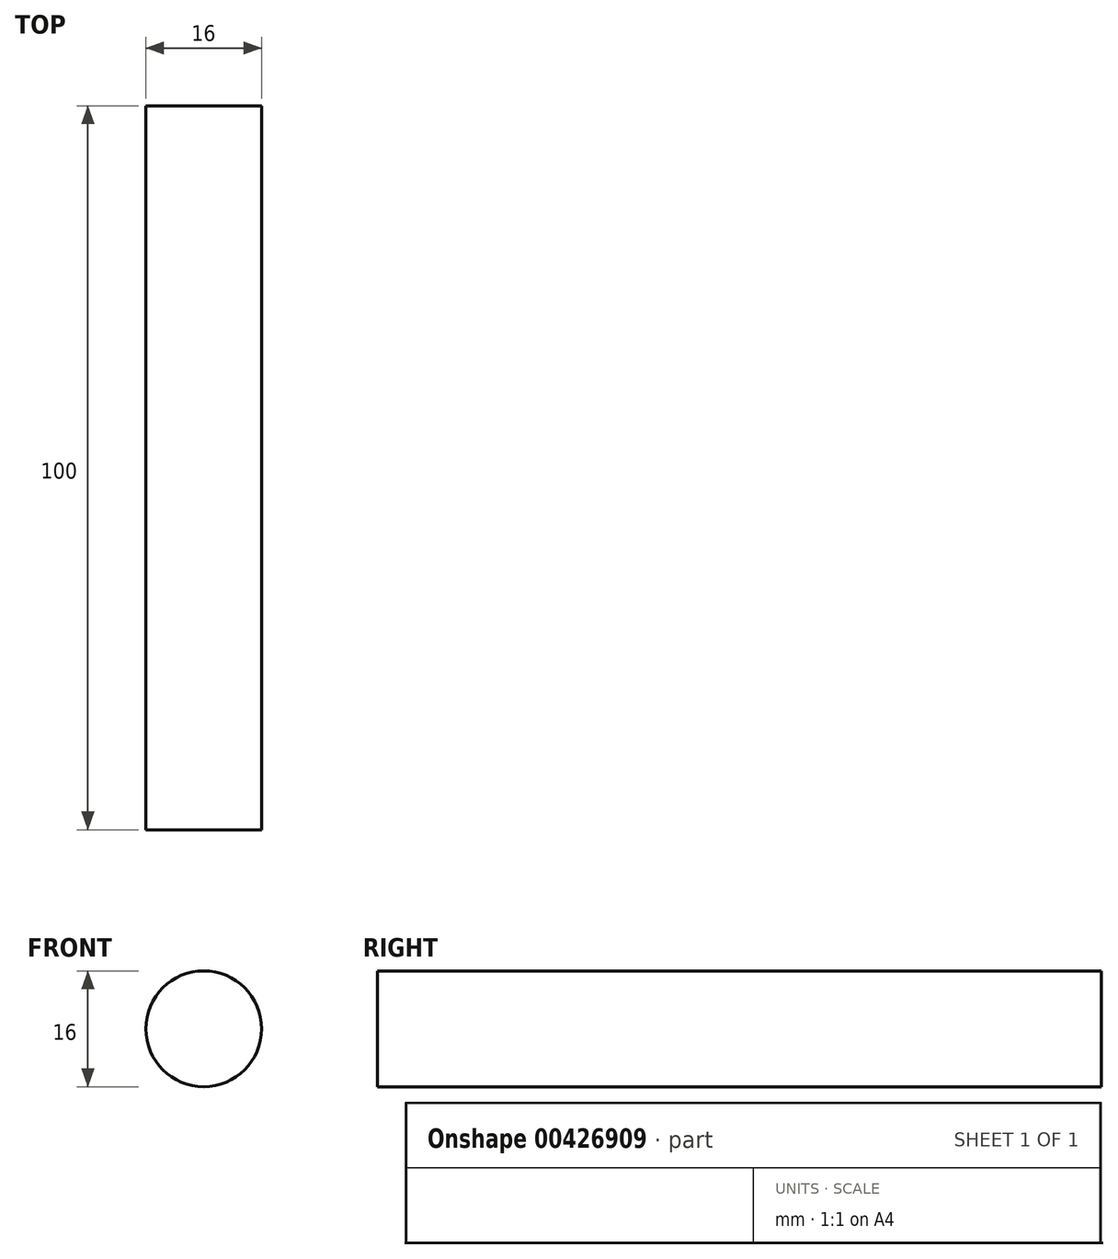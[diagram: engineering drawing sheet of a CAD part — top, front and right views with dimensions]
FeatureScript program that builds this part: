
annotation { "Feature Type Name" : "Feature", "Feature Type Description" : "" }
export const myFeature = defineFeature(function(context is Context, id is Id, definition is map)
    precondition{}
    {
        {
            var Q0;
            Q0=qCreatedBy(makeId("Front.planeOp"),FACE);
            var sketch = newSketch(context, id + "F0", { "sketchPlane" : qUnion([Q0])});
            skCircle(sketch, "E0", {"center": v(-49.99, 49.8) * mm, "radius": 8 * mm});
            skSolve(sketch);
        }
        {
            var Q0;
            Q0=makeQuery(id+"F0.imprint","IMPRINT",FACE,{"disambiguationData":[TD([[makeQuery(id+"F0.imprint","IMPRINT",EDGE,{"derivedFrom":sQuery(id+"F0.wireOp",EDGE,"E0")}),1.0]])]});
            extrude(context, id + "F1", {"entities" : qUnion([Q0]), "depth" : 100 * mm});
        }
    });
